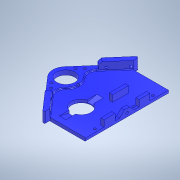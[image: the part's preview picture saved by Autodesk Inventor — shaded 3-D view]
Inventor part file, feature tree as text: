
AUTODESK INVENTOR PART (.ipt)
format: ipt  version: 2022 (Build 260153000, 153)  size: 485,376 bytes
history: native  units: in
note: dims shown in document units (in); Inventor stores cm internally (conversion verified against a paired STEP export)
features: sketch x14, extrude x10, reference x9, projected_geometry x6, other x6, hole x4, fillet x2, chamfer x2, mirror x1, revolve x1, pattern_circular x1
ambient origin geometry x8: Origin, YZ Plane, XZ Plane, XY Plane, X Axis, Y Axis, Z Axis, Center Point
bodies: Solid3 (feature_tree)
feature tree (56):
  extrude  "Extrusion13"  Depth=2.1654in
  extrude  "Extrusion14"  Depth=1.7717in TaperAngle=0.0deg
  mirror  "Mirror4"
  extrude  "Extrusion25"  Depth=0.1969in TaperAngle=0.0deg
  extrude  "Extrusion26"  Depth=1.5748in
  extrude  "Extrusion28"  Depth=0.1969in
  extrude  "Extrusion35"  Depth=0.5906in
  extrude  "Extrusion38"  Depth=1.1811in
  extrude  "Extrusion39"  TaperAngle=0.0deg  [1 undecoded]
  hole  "Hole5"  [1 undecoded]
  fillet  "Fillet3"  [1 undecoded]
  fillet  "Fillet4"  Radius=1.5354in
  hole  "Hole6"  [1 undecoded]
  hole  "Hole7"  [1 undecoded]
  chamfer  "Chamfer3"  Distance=0.3937in
  chamfer  "Chamfer4"  Distance=0.3937in
  extrude  "Extrusion40"  Depth=0.9055in
  hole  "Hole8"  [1 undecoded]
  extrude  "Extrusion41"  Depth=0.1969in
  revolve  "Revolution1"  [1 undecoded]
  pattern_circular  "Circular Pattern1"  Count=3  [1 undecoded]
  sketch  "Sketch14"  dims[d94=0.9646in d95=2.1654in]
  sketch  "Sketch15"  dims[d96=1.7717in d97=0.4433in d98=0.0in]
  projected_geometry  "Projected Loop7"
  sketch  "Sketch26"  dims[d99=2.5561in d100=0.1969in d101=0.0in]
  sketch  "Sketch29"  dims[d137=0.7874in d138=1.5748in]
  sketch  "Sketch37"  dims[d139=0.1969in d140=0.0in d141=1.1024in]
  projected_geometry  "Projected Loop19"
  sketch  "Sketch40"  dims[d143=0.0787in d144=0.0in d145=0.5906in]
  projected_geometry  "Projected Loop20"
  sketch  "Sketch41"  dims[d146=1.1024in d151=1.1811in]
  projected_geometry  "Projected Loop21"
  sketch  "Sketch42"  dims[d152=0.3937in d153=0.0in d185=0.0in d186=0.0in]
  projected_geometry  "Projected Loop22"
  sketch  "Sketch43"  dims[d198=0.4724in d199=0.4724in d200=0.0in d201=0.0in d202=1.5354in]
  reference  "Reference1"
  reference  "Reference2"
  sketch  "Sketch44"  dims[d203=1.7717in d204=1.8504in]
  reference  "Reference3"
  reference  "Reference4"
  sketch  "Sketch45"  dims[d205=0.3937in d206=0.0in d207=1.8504in]
  sketch  "Sketch46"  dims[d208=0.3937in]
  reference  "Reference5"
  sketch  "Sketch47"  dims[d209=0.3937in]
  reference  "Reference6"
  reference  "Reference7"
  projected_geometry  "Projected Loop23"
  reference  "Reference8"
  reference  "Reference9"
  sketch  "Sketch49"  dims[d210=0.9449in d211=0.3937in d213=0.3937in d214=0.9055in d215=0.9055in d216=0.1969in d217=0.1969in d220=1.1811in d221=1.1811in d222=1.1811in d223=0.7553in d224=0.7553in d225=1.1811in d226=0.1575in d227=0.2362in d228=0.248in d229=0.0787in d230=90.0deg d231=0.2756in d232=0.0in d233=0.0787in d234=0.0394in d235=0.1575in d236=0.2362in d237=0.1575in d238=0.0787in d239=90.0deg d240=0.315in d241=0.8108in d242=0.1575in d243=0.2362in d244=0.1575in d245=0.0787in d246=90.0deg d247=0.315in d248=0.8108in d249=0.0394in d250=0.0787in d251=45.0deg d252=0.1575in d253=0.0787in d254=45.0deg d255=0.2913in d256=0.315in d257=135.0deg d258=0.1969in d259=0.0in d260=0.1575in d261=0.2362in d262=0.1575in d263=0.0787in d264=90.0deg d265=0.315in d266=0.0in d268=0.1417in d269=0.1417in d270=0.9843in d271=0.1969in d273=0.1417in d274=0.1417in d275=0.3937in d276=0.0in d277=0.1181in d278=0.1969in d279=0.1969in d280=0.1181in d289=0.3937in d290=0.5906in d291=15.0deg d292=0.7874in d293=360.0deg d93=0.1575in d107=0.0197in d108=0.0344in d109=0.0197in d110=0.0344in d154=0.0197in d155=0.0344in d294=0.0344in]
  parser-record x1  (decoder bookkeeping rows leaked as tree rows — omitted from the tree; the rows remain in map.json)
  other  "Main Body.iam"
  other  "Front Armor:2"
  other  "Front Armor:1"
  other  "Base Plate:2"
  other  "Battery:1"
note: 8 required parameter values undecoded (feature->parameter linkage not recoverable at this tier; creation-order binding heuristic only, values carry confidence <= 0.55)
note: 1 file-system path scrubbed to <path> (originals preserved in map.json)